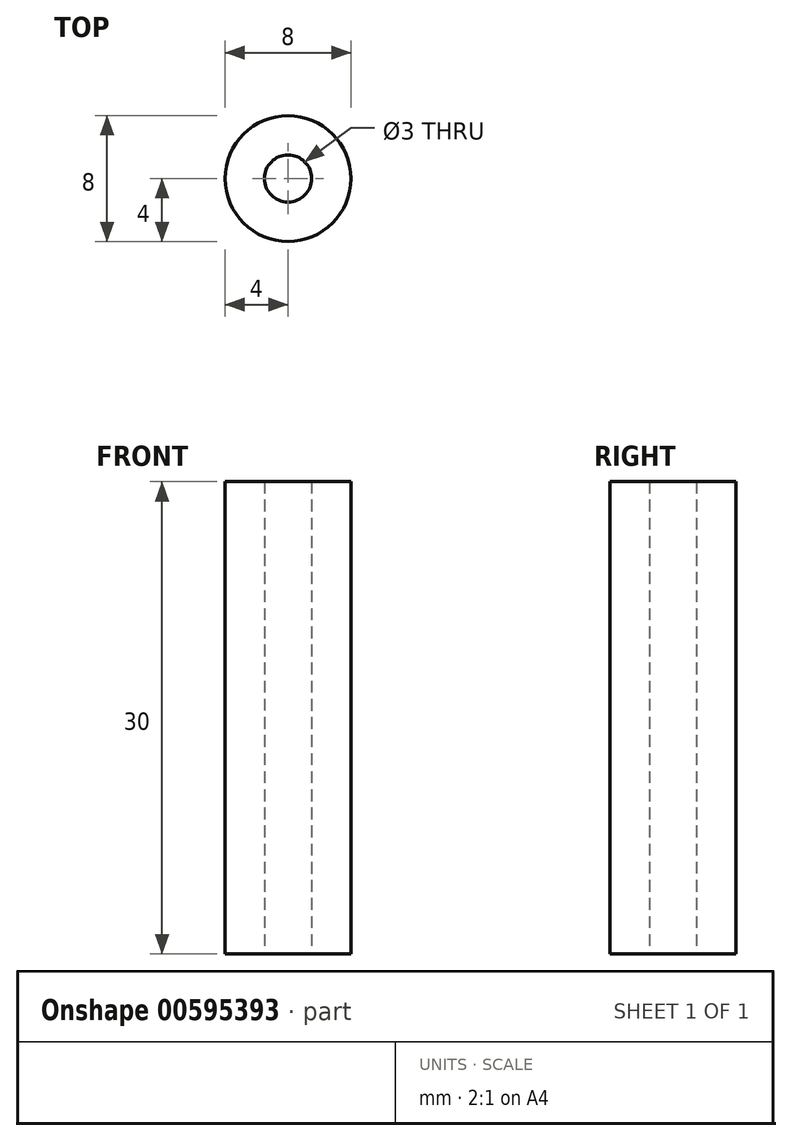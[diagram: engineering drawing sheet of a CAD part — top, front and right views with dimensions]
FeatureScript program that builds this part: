
annotation { "Feature Type Name" : "Feature", "Feature Type Description" : "" }
export const myFeature = defineFeature(function(context is Context, id is Id, definition is map)
    precondition{}
    {
        {
            var Q0;
            Q0=qCreatedBy(makeId("Top.planeOp"),FACE);
            var sketch = newSketch(context, id + "F0", { "sketchPlane" : qUnion([Q0])});
            skCircle(sketch, "E0", {"center": v(0, 0) * mm, "radius": 4 * mm});
            skCircle(sketch, "E1", {"center": v(0, 0) * mm, "radius": 1.5 * mm});
            skSolve(sketch);
        }
        {
            var Q0;
            Q0 = qSketchRegion(id + "F0", true);
            extrude(context, id + "F1", {"entities" : qUnion([Q0]), "depth" : 30 * mm, "offsetDistance" : 25 * mm});
        }
    });
